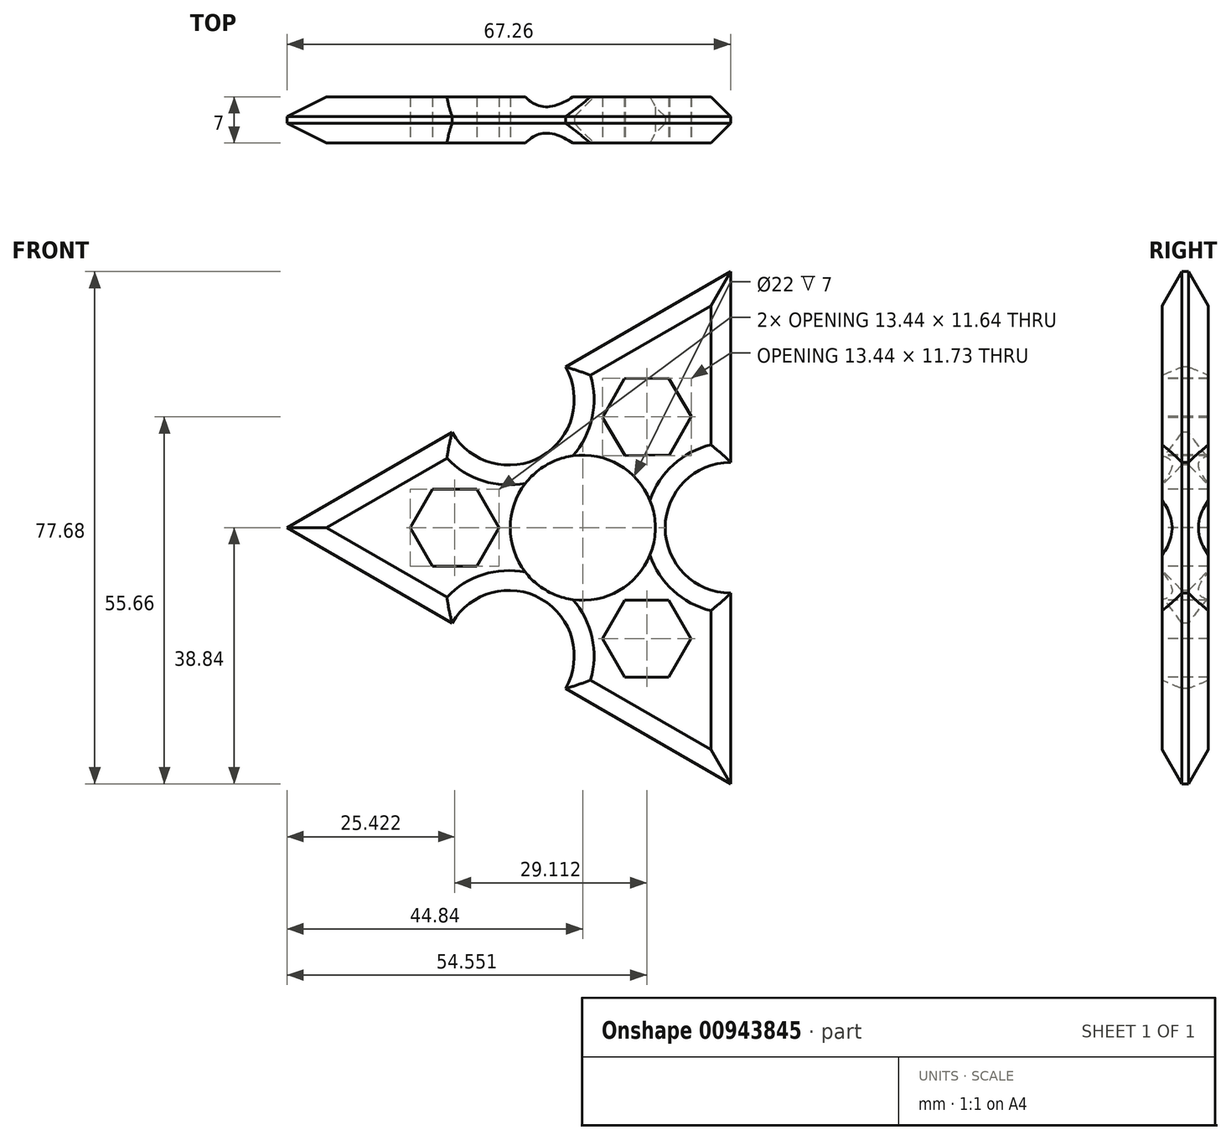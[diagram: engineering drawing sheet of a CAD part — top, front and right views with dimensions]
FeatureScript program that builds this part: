
annotation { "Feature Type Name" : "Feature", "Feature Type Description" : "" }
export const myFeature = defineFeature(function(context is Context, id is Id, definition is map)
    precondition{}
    {
        {
            var Q0;
            Q0=qCreatedBy(makeId("Front.planeOp"),FACE);
            var sketch = newSketch(context, id + "F0", { "sketchPlane" : qUnion([Q0])});
            skCircle(sketch, "E0.cCircle", {"center": v(0, 0) * mm, "radius": 44.84 * mm, "construction": true});
            skLineSegment(sketch, "E0.0", {"start": v(-44.84, 0) * mm, "end": v(22.42, 38.84) * mm});
            skLineSegment(sketch, "E0.1", {"start": v(22.42, 38.84) * mm, "end": v(22.42, -38.84) * mm});
            skLineSegment(sketch, "E0.2", {"start": v(22.42, -38.84) * mm, "end": v(-44.84, 0) * mm});
            skPoint(sketch, "E1", {"position": v(22.42, 0) * mm});
            skPoint(sketch, "E2", {"position": v(-11.21, 19.42) * mm});
            skPoint(sketch, "E3", {"position": v(-11.21, -19.42) * mm});
            skCircle(sketch, "E4", {"center": v(22.42, 0) * mm, "radius": 9.92 * mm});
            skCircle(sketch, "E5", {"center": v(-11.21, 19.42) * mm, "radius": 9.92 * mm});
            skCircle(sketch, "E6", {"center": v(-11.21, -19.42) * mm, "radius": 9.92 * mm});
            skCircle(sketch, "E7", {"center": v(0, 0) * mm, "radius": 11 * mm});
            skSolve(sketch);
        }
        {
            var Q0;
            {var subQ5=sQuery(id+"F0.wireOp",EDGE,"FH4wdCUx-9VzK-oPog-yWks-AWr1iO5oHcZ7");var subQ7=sQuery(id+"F0.wireOp",EDGE,"E4");var subQ9=makeQuery(id+"F0.imprint","INTERSECT",VERTEX,{"derivedFrom":[subQ5,subQ7]});Q0=makeQuery(id+"F0.imprint","IMPRINT",FACE,{"disambiguationData":[TD([[makeQuery(id+"F0.imprint","IMPRINT",EDGE,{"disambiguationData":[TD([[subQ9,1.0]])],"derivedFrom":subQ5}),-1.0]])]});}
            var Q1;
            {var subQ3=sQuery(id+"F0.wireOp",EDGE,"E5");var subQ5=sQuery(id+"F0.wireOp",EDGE,"FH4wdCUx-9VzK-oPog-yWks-AWr1iO5oHcZ7");var subQ6=makeQuery(id+"F0.imprint","INTERSECT",VERTEX,{"derivedFrom":[subQ5,subQ3]});Q1=makeQuery(id+"F0.imprint","IMPRINT",FACE,{"disambiguationData":[TD([[makeQuery(id+"F0.imprint","IMPRINT",EDGE,{"disambiguationData":[TD([[subQ6,-1.0]])],"derivedFrom":subQ5}),-1.0]])]});}
            var Q2;
            {var subQ3=sQuery(id+"F0.wireOp",EDGE,"FH4wdCUx-9VzK-oPog-yWks-AWr1iO5oHcZ7");var subQ7=sQuery(id+"F0.wireOp",EDGE,"E5");var subQ9=makeQuery(id+"F0.imprint","INTERSECT",VERTEX,{"derivedFrom":[subQ3,subQ7]});Q2=makeQuery(id+"F0.imprint","IMPRINT",FACE,{"disambiguationData":[TD([[makeQuery(id+"F0.imprint","IMPRINT",EDGE,{"disambiguationData":[TD([[subQ9,1.0]])],"derivedFrom":subQ3}),-1.0]])]});}
            var Q3;
            Q3=makeQuery(id+"F0.imprint","IMPRINT",FACE,{"disambiguationData":[TD([[makeQuery(id+"F0.imprint","IMPRINT",EDGE,{"derivedFrom":sQuery(id+"F0.wireOp",EDGE,"E7")}),-1.0]])]});
            extrude(context, id + "F1", {"entities" : qUnion([Q0, Q1, Q2, Q3]), "oppositeDirection" : true, "depth" : 7 * mm, "offsetDistance" : 25.4 * mm});
        }
        {
            var Q0;
            Q0=makeQuery(id+"F1.opExtrude","CAP_EDGE",EDGE,{"disambiguationData":[OSD([sQuery(id+"F0.wireOp",EDGE,"E5")])],"isStart":true});
            var Q1;
            Q1=makeQuery(id+"F1.opExtrude","CAP_EDGE",EDGE,{"disambiguationData":[OSD([sQuery(id+"F0.wireOp",EDGE,"E5")])],"isStart":false});
            var Q2;
            {var subQ0=sQuery(id+"F0.wireOp",EDGE,"E0.0");Q2=makeQuery(id+"F1.opExtrude","CAP_EDGE",EDGE,{"disambiguationData":[OSD([subQ0]),TDD([makeQuery(id+"F0.imprint","IMPRINT",EDGE,{"disambiguationData":[TD([[makeQuery(id+"F0.imprint","INTERSECT",VERTEX,{"derivedFrom":[subQ0,sQuery(id+"F0.wireOp",EDGE,"E0.1")]}),1.0]])],"derivedFrom":subQ0})])],"isStart":false});}
            var Q3;
            {var subQ0=sQuery(id+"F0.wireOp",EDGE,"E0.0");Q3=makeQuery(id+"F1.opExtrude","CAP_EDGE",EDGE,{"disambiguationData":[OSD([subQ0]),TDD([makeQuery(id+"F0.imprint","IMPRINT",EDGE,{"disambiguationData":[TD([[makeQuery(id+"F0.imprint","INTERSECT",VERTEX,{"derivedFrom":[subQ0,sQuery(id+"F0.wireOp",EDGE,"E0.1")]}),1.0]])],"derivedFrom":subQ0})])],"isStart":true});}
            var Q4;
            {var subQ0=sQuery(id+"F0.wireOp",EDGE,"E0.0");Q4=makeQuery(id+"F1.opExtrude","CAP_EDGE",EDGE,{"disambiguationData":[OSD([subQ0]),TDD([makeQuery(id+"F0.imprint","IMPRINT",EDGE,{"disambiguationData":[TD([[makeQuery(id+"F0.imprint","INTERSECT",VERTEX,{"derivedFrom":[subQ0,sQuery(id+"F0.wireOp",EDGE,"E0.2")]}),-1.0]])],"derivedFrom":subQ0})])],"isStart":true});}
            var Q5;
            {var subQ0=sQuery(id+"F0.wireOp",EDGE,"E0.0");Q5=makeQuery(id+"F1.opExtrude","CAP_EDGE",EDGE,{"disambiguationData":[OSD([subQ0]),TDD([makeQuery(id+"F0.imprint","IMPRINT",EDGE,{"disambiguationData":[TD([[makeQuery(id+"F0.imprint","INTERSECT",VERTEX,{"derivedFrom":[subQ0,sQuery(id+"F0.wireOp",EDGE,"E0.2")]}),-1.0]])],"derivedFrom":subQ0})])],"isStart":false});}
            var Q6;
            {var subQ0=sQuery(id+"F0.wireOp",EDGE,"E0.2");Q6=makeQuery(id+"F1.opExtrude","CAP_EDGE",EDGE,{"disambiguationData":[OSD([subQ0]),TDD([makeQuery(id+"F0.imprint","IMPRINT",EDGE,{"disambiguationData":[TD([[makeQuery(id+"F0.imprint","INTERSECT",VERTEX,{"derivedFrom":[sQuery(id+"F0.wireOp",EDGE,"E0.0"),subQ0]}),1.0]])],"derivedFrom":subQ0})])],"isStart":true});}
            var Q7;
            {var subQ0=sQuery(id+"F0.wireOp",EDGE,"E0.2");Q7=makeQuery(id+"F1.opExtrude","CAP_EDGE",EDGE,{"disambiguationData":[OSD([subQ0]),TDD([makeQuery(id+"F0.imprint","IMPRINT",EDGE,{"disambiguationData":[TD([[makeQuery(id+"F0.imprint","INTERSECT",VERTEX,{"derivedFrom":[sQuery(id+"F0.wireOp",EDGE,"E0.0"),subQ0]}),1.0]])],"derivedFrom":subQ0})])],"isStart":false});}
            var Q8;
            Q8=makeQuery(id+"F1.opExtrude","CAP_EDGE",EDGE,{"disambiguationData":[OSD([sQuery(id+"F0.wireOp",EDGE,"E6")])],"isStart":true});
            var Q9;
            Q9=makeQuery(id+"F1.opExtrude","CAP_EDGE",EDGE,{"disambiguationData":[OSD([sQuery(id+"F0.wireOp",EDGE,"E6")])],"isStart":false});
            var Q10;
            {var subQ0=sQuery(id+"F0.wireOp",EDGE,"E0.2");Q10=makeQuery(id+"F1.opExtrude","CAP_EDGE",EDGE,{"disambiguationData":[OSD([subQ0]),TDD([makeQuery(id+"F0.imprint","IMPRINT",EDGE,{"disambiguationData":[TD([[makeQuery(id+"F0.imprint","INTERSECT",VERTEX,{"derivedFrom":[sQuery(id+"F0.wireOp",EDGE,"E0.1"),subQ0]}),-1.0]])],"derivedFrom":subQ0})])],"isStart":true});}
            var Q11;
            {var subQ0=sQuery(id+"F0.wireOp",EDGE,"E0.2");Q11=makeQuery(id+"F1.opExtrude","CAP_EDGE",EDGE,{"disambiguationData":[OSD([subQ0]),TDD([makeQuery(id+"F0.imprint","IMPRINT",EDGE,{"disambiguationData":[TD([[makeQuery(id+"F0.imprint","INTERSECT",VERTEX,{"derivedFrom":[sQuery(id+"F0.wireOp",EDGE,"E0.1"),subQ0]}),-1.0]])],"derivedFrom":subQ0})])],"isStart":false});}
            var Q12;
            {var subQ0=sQuery(id+"F0.wireOp",EDGE,"E0.1");Q12=makeQuery(id+"F1.opExtrude","CAP_EDGE",EDGE,{"disambiguationData":[OSD([subQ0]),TDD([makeQuery(id+"F0.imprint","IMPRINT",EDGE,{"disambiguationData":[TD([[makeQuery(id+"F0.imprint","INTERSECT",VERTEX,{"derivedFrom":[subQ0,sQuery(id+"F0.wireOp",EDGE,"E0.2")]}),1.0]])],"derivedFrom":subQ0})])],"isStart":true});}
            var Q13;
            {var subQ0=sQuery(id+"F0.wireOp",EDGE,"E0.1");Q13=makeQuery(id+"F1.opExtrude","CAP_EDGE",EDGE,{"disambiguationData":[OSD([subQ0]),TDD([makeQuery(id+"F0.imprint","IMPRINT",EDGE,{"disambiguationData":[TD([[makeQuery(id+"F0.imprint","INTERSECT",VERTEX,{"derivedFrom":[subQ0,sQuery(id+"F0.wireOp",EDGE,"E0.2")]}),1.0]])],"derivedFrom":subQ0})])],"isStart":false});}
            var Q14;
            Q14=makeQuery(id+"F1.opExtrude","CAP_EDGE",EDGE,{"disambiguationData":[OSD([sQuery(id+"F0.wireOp",EDGE,"E4")])],"isStart":true});
            var Q15;
            Q15=makeQuery(id+"F1.opExtrude","CAP_EDGE",EDGE,{"disambiguationData":[OSD([sQuery(id+"F0.wireOp",EDGE,"E4")])],"isStart":false});
            var Q16;
            {var subQ0=sQuery(id+"F0.wireOp",EDGE,"E0.1");Q16=makeQuery(id+"F1.opExtrude","CAP_EDGE",EDGE,{"disambiguationData":[OSD([subQ0]),TDD([makeQuery(id+"F0.imprint","IMPRINT",EDGE,{"disambiguationData":[TD([[makeQuery(id+"F0.imprint","INTERSECT",VERTEX,{"derivedFrom":[sQuery(id+"F0.wireOp",EDGE,"E0.0"),subQ0]}),-1.0]])],"derivedFrom":subQ0})])],"isStart":true});}
            var Q17;
            {var subQ0=sQuery(id+"F0.wireOp",EDGE,"E0.1");Q17=makeQuery(id+"F1.opExtrude","CAP_EDGE",EDGE,{"disambiguationData":[OSD([subQ0]),TDD([makeQuery(id+"F0.imprint","IMPRINT",EDGE,{"disambiguationData":[TD([[makeQuery(id+"F0.imprint","INTERSECT",VERTEX,{"derivedFrom":[sQuery(id+"F0.wireOp",EDGE,"E0.0"),subQ0]}),-1.0]])],"derivedFrom":subQ0})])],"isStart":false});}
            chamfer(context, id + "F2", {"entities" : qUnion([Q0, Q1, Q2, Q3, Q4, Q5, Q6, Q7, Q8, Q9, Q10, Q11, Q12, Q13, Q14, Q15, Q16, Q17]), "chamferType" : ChamferType.TWO_OFFSETS, "width1" : 3 * mm, "oppositeDirection" : false, "width2" : 3 * mm, "tangentPropagation" : true});
        }
        {
            var Q0;
            Q0=makeQuery(id+"F2.opChamfer","SPLIT",FACE,{"disambiguationData":[OD(0.0)],"derivedFrom":makeQuery(id+"F1.opExtrude","CAP_FACE",FACE,{"disambiguationData":[OSD([sQuery(id+"F0.wireOp",EDGE,"E0.0"),sQuery(id+"F0.wireOp",EDGE,"E0.1"),sQuery(id+"F0.wireOp",EDGE,"E0.2"),sQuery(id+"F0.wireOp",EDGE,"E4"),sQuery(id+"F0.wireOp",EDGE,"E5"),sQuery(id+"F0.wireOp",EDGE,"E6"),sQuery(id+"F0.wireOp",EDGE,"E7")])],"isStart":true})});
            var sketch = newSketch(context, id + "F3", { "sketchPlane" : qUnion([Q0])});
            skLineSegment(sketch, "E8", {"start": v(0, 0) * mm, "end": v(19.42, 33.64) * mm});
            skLineSegment(sketch, "E9", {"start": v(-38.84, 0) * mm, "end": v(0, 0) * mm});
            skPoint(sketch, "E10", {"position": v(9.71, 16.82) * mm});
            skPoint(sketch, "E11", {"position": v(-19.42, 0) * mm});
            skCircle(sketch, "E12.cCircle", {"center": v(9.71, 16.82) * mm, "radius": 5.82 * mm, "construction": true});
            skLineSegment(sketch, "E12.0", {"start": v(16.43, 16.9) * mm, "end": v(13.15, 11.04) * mm});
            skLineSegment(sketch, "E12.1", {"start": v(13.15, 11.04) * mm, "end": v(6.42, 10.96) * mm});
            skLineSegment(sketch, "E12.2", {"start": v(6.42, 10.96) * mm, "end": v(2.99, 16.73) * mm});
            skLineSegment(sketch, "E12.3", {"start": v(2.99, 16.73) * mm, "end": v(6.27, 22.6) * mm});
            skLineSegment(sketch, "E12.4", {"start": v(6.27, 22.6) * mm, "end": v(13, 22.69) * mm});
            skLineSegment(sketch, "E12.5", {"start": v(13, 22.69) * mm, "end": v(16.43, 16.9) * mm});
            skCircle(sketch, "E13.cCircle", {"center": v(-19.42, 0) * mm, "radius": 5.82 * mm, "construction": true});
            skLineSegment(sketch, "E13.0", {"start": v(-12.7, 0) * mm, "end": v(-16.06, -5.82) * mm});
            skLineSegment(sketch, "E13.1", {"start": v(-16.06, -5.82) * mm, "end": v(-22.78, -5.82) * mm});
            skLineSegment(sketch, "E13.2", {"start": v(-22.78, -5.82) * mm, "end": v(-26.14, 0) * mm});
            skLineSegment(sketch, "E13.3", {"start": v(-26.14, 0) * mm, "end": v(-22.78, 5.82) * mm});
            skLineSegment(sketch, "E13.4", {"start": v(-22.78, 5.82) * mm, "end": v(-16.06, 5.82) * mm});
            skLineSegment(sketch, "E13.5", {"start": v(-16.06, 5.82) * mm, "end": v(-12.7, 0) * mm});
            skPoint(sketch, "E13.0.midPoint", {"position": v(-14.38, -2.9) * mm});
            skLineSegment(sketch, "E14", {"start": v(19.39, -33.65) * mm, "end": v(0, 0) * mm});
            skPoint(sketch, "E15", {"position": v(9.7, -16.83) * mm});
            skCircle(sketch, "E16.cCircle", {"center": v(9.7, -16.83) * mm, "radius": 5.82 * mm, "construction": true});
            skLineSegment(sketch, "E16.0", {"start": v(6.33, -22.64) * mm, "end": v(2.98, -16.82) * mm});
            skLineSegment(sketch, "E16.1", {"start": v(2.98, -16.82) * mm, "end": v(6.34, -11) * mm});
            skLineSegment(sketch, "E16.2", {"start": v(6.34, -11) * mm, "end": v(13.06, -11.01) * mm});
            skLineSegment(sketch, "E16.3", {"start": v(13.06, -11.01) * mm, "end": v(16.41, -16.83) * mm});
            skLineSegment(sketch, "E16.4", {"start": v(16.41, -16.83) * mm, "end": v(13.05, -22.65) * mm});
            skLineSegment(sketch, "E16.5", {"start": v(13.05, -22.65) * mm, "end": v(6.33, -22.64) * mm});
            skPoint(sketch, "E16.0.midPoint", {"position": v(4.65, -19.73) * mm});
            skSolve(sketch);
        }
        {
            var Q0;
            {var subQ4=sQuery(id+"F3.wireOp",EDGE,"E12.0");Q0=makeQuery(id+"F3.imprint","IMPRINT",FACE,{"disambiguationData":[TD([[makeQuery(id+"F3.imprint","IMPRINT",EDGE,{"derivedFrom":subQ4}),-1.0]])]});}
            var Q1;
            {var subQ1=sQuery(id+"F3.wireOp",EDGE,"E12.3");Q1=makeQuery(id+"F3.imprint","IMPRINT",FACE,{"disambiguationData":[TD([[makeQuery(id+"F3.imprint","IMPRINT",EDGE,{"derivedFrom":subQ1}),-1.0]])]});}
            var Q2;
            {var subQ0=sQuery(id+"F3.wireOp",EDGE,"dd589d58-721f-4d6e-b9c3-ca4471d38528.4");Q2=makeQuery(id+"F3.imprint","IMPRINT",FACE,{"disambiguationData":[TD([[makeQuery(id+"F3.imprint","IMPRINT",EDGE,{"derivedFrom":subQ0}),-1.0]])]});}
            var Q3;
            {var subQ1=sQuery(id+"F3.wireOp",EDGE,"dd589d58-721f-4d6e-b9c3-ca4471d38528.1");Q3=makeQuery(id+"F3.imprint","IMPRINT",FACE,{"disambiguationData":[TD([[makeQuery(id+"F3.imprint","IMPRINT",EDGE,{"derivedFrom":subQ1}),-1.0]])]});}
            var Q4;
            {var subQ2=sQuery(id+"F3.wireOp",EDGE,"E13.3");Q4=makeQuery(id+"F3.imprint","IMPRINT",FACE,{"disambiguationData":[TD([[makeQuery(id+"F3.imprint","IMPRINT",EDGE,{"derivedFrom":subQ2}),-1.0]])]});}
            var Q5;
            {var subQ0=sQuery(id+"F3.wireOp",EDGE,"E13.0");Q5=makeQuery(id+"F3.imprint","IMPRINT",FACE,{"disambiguationData":[TD([[makeQuery(id+"F3.imprint","IMPRINT",EDGE,{"derivedFrom":subQ0}),-1.0]])]});}
            extrude(context, id + "F4", {"entities" : qUnion([Q0, Q1, Q2, Q3, Q4, Q5]), "operationType" : NewBodyOperationType.REMOVE, "oppositeDirection" : true, "depth" : 25.4 * mm, "offsetDistance" : 25.4 * mm});
        }
        {
            var Q0;
            Q0 = qSketchRegion(id + "F3", true);
            extrude(context, id + "F5", {"entities" : qUnion([Q0]), "operationType" : NewBodyOperationType.REMOVE, "oppositeDirection" : true, "depth" : 25.4 * mm, "offsetDistance" : 25.4 * mm});
        }
    });
